# Revit family: PGR_Noken_Bths_Acore
name_source: partatom
category: Plumbing Fixtures
revit_build: Autodesk Revit 2017 (Build: 20181011_1645(x64)
units: mm (PartAtom-declared; Revit-internal decimal feet)

## family parameters
Cut with Voids When Loaded = No
Host = Face
OmniClass Number = 23.45.05.14.21
OmniClass Title = Bathtubs
Part Type = Normal
Room Calculation Point = No
Round Connector Dimension = Use Diameter
Shared = No

## types (5) — shared parameters
AccessibilityPerformance = See ProductInformation for technical PDF
AssetType = Fixed
BIMObjectName = PGR_Noken_Baths_Acore_White-1200x700x400mm-100050752
BathType = Domestic
Category = Pr_40_20_06_08: Baths
CodePerformance = UNE EN 14516
Collection = Acore
Color = White
Description = Bathtub, built-in version, without brassware, rectangular 120x70, side bath waste not included, 102 L water capacity, 2,2mm enamelled steel. UNE EN 14516. 2 years warranty.
DrainSize = 52
DurationUnit = Year
Features = See ProductInformation for technical PDF
Finish = White
FlowRate = 102 L
HasGrabHandles = No
IfcExportAs = IfcSanitaryTerminalType
IfcExportType = Bath
ManufacturerURL = ww.noken.com
Material = Enameled  steel
MaterialCeramic = PGR_Noken_Porcelain
MaterialMetal = PGR_Noken_Brass_Chrome
MaterialThickness = 2 mm  [stored 0.00656168 ft]
Model = 100050752
ModelNumber = 100050752
ModelReference = ACORE 120X70 BASIC BB
NBSDescription = Baths
NBSReference = 45-35-70/311
Name = Baths_Acore_White-1200x700x400mm-100050752
NominalDepth = 400 mm  [stored 1.31234 ft]
NominalHeight = 400 mm  [stored 1.31234 ft]
NominalWidth = 700 mm  [stored 2.29659 ft]
Overflow = No
ProductInformation = http://calidad.info-grupo.com:8081
Reference = -
Shape = Rectangular
Status = UNSET
SustainabilityPerformance = See ProductInformation for technical PDF
TapHoles = 0
TechnicalDrawing = See ProductInformation for technical PDF
Type Image = 100050760.jpg
URL = www.noken.com
Uniclass2015Code = Pr_40_20_06_08
Uniclass2015Title = Baths
Uniclass2015Version = V1_8
Version = 1
WarrantyDescription = See ProductInformation for technical PDF
WarrantyDurationParts = See ProductInformation for technical PDF
WarrantyDurationUnit = See ProductInformation for technical PDF
zero-valued in all types: Default Elevation, Height, WFU

## per-type parameters (varying)
| type | NettWeight | NominalLength | Size |
| 1200x700mm-100050752 | 16 | 1200 mm | 1200x700x400mm |
| 1400x700mm-100050754 | 19.2 | 1400 mm  [stored 4.59318 ft] | 1400x700x400mm |
| 1500x700mm-100050756 | 20.8 | 1500 mm  [stored 4.92126 ft] | 1500x700x400mm |
| 1600x700mm-100050758 | 21.5 | 1600 mm  [stored 5.24934 ft] | 1600x700x400mm |
| 1700x700mm-100050760 | 23.5 | 1700 mm  [stored 5.57743 ft] | 1700x700x400mm |

note: [stored X ft] marks values corroborated as IEEE doubles in the binary element streams (Revit-internal decimal feet)

## geometry (parser evidence)
native form markers: Blend x2, Sweep x3
no freeform markers — native parametric forms only
